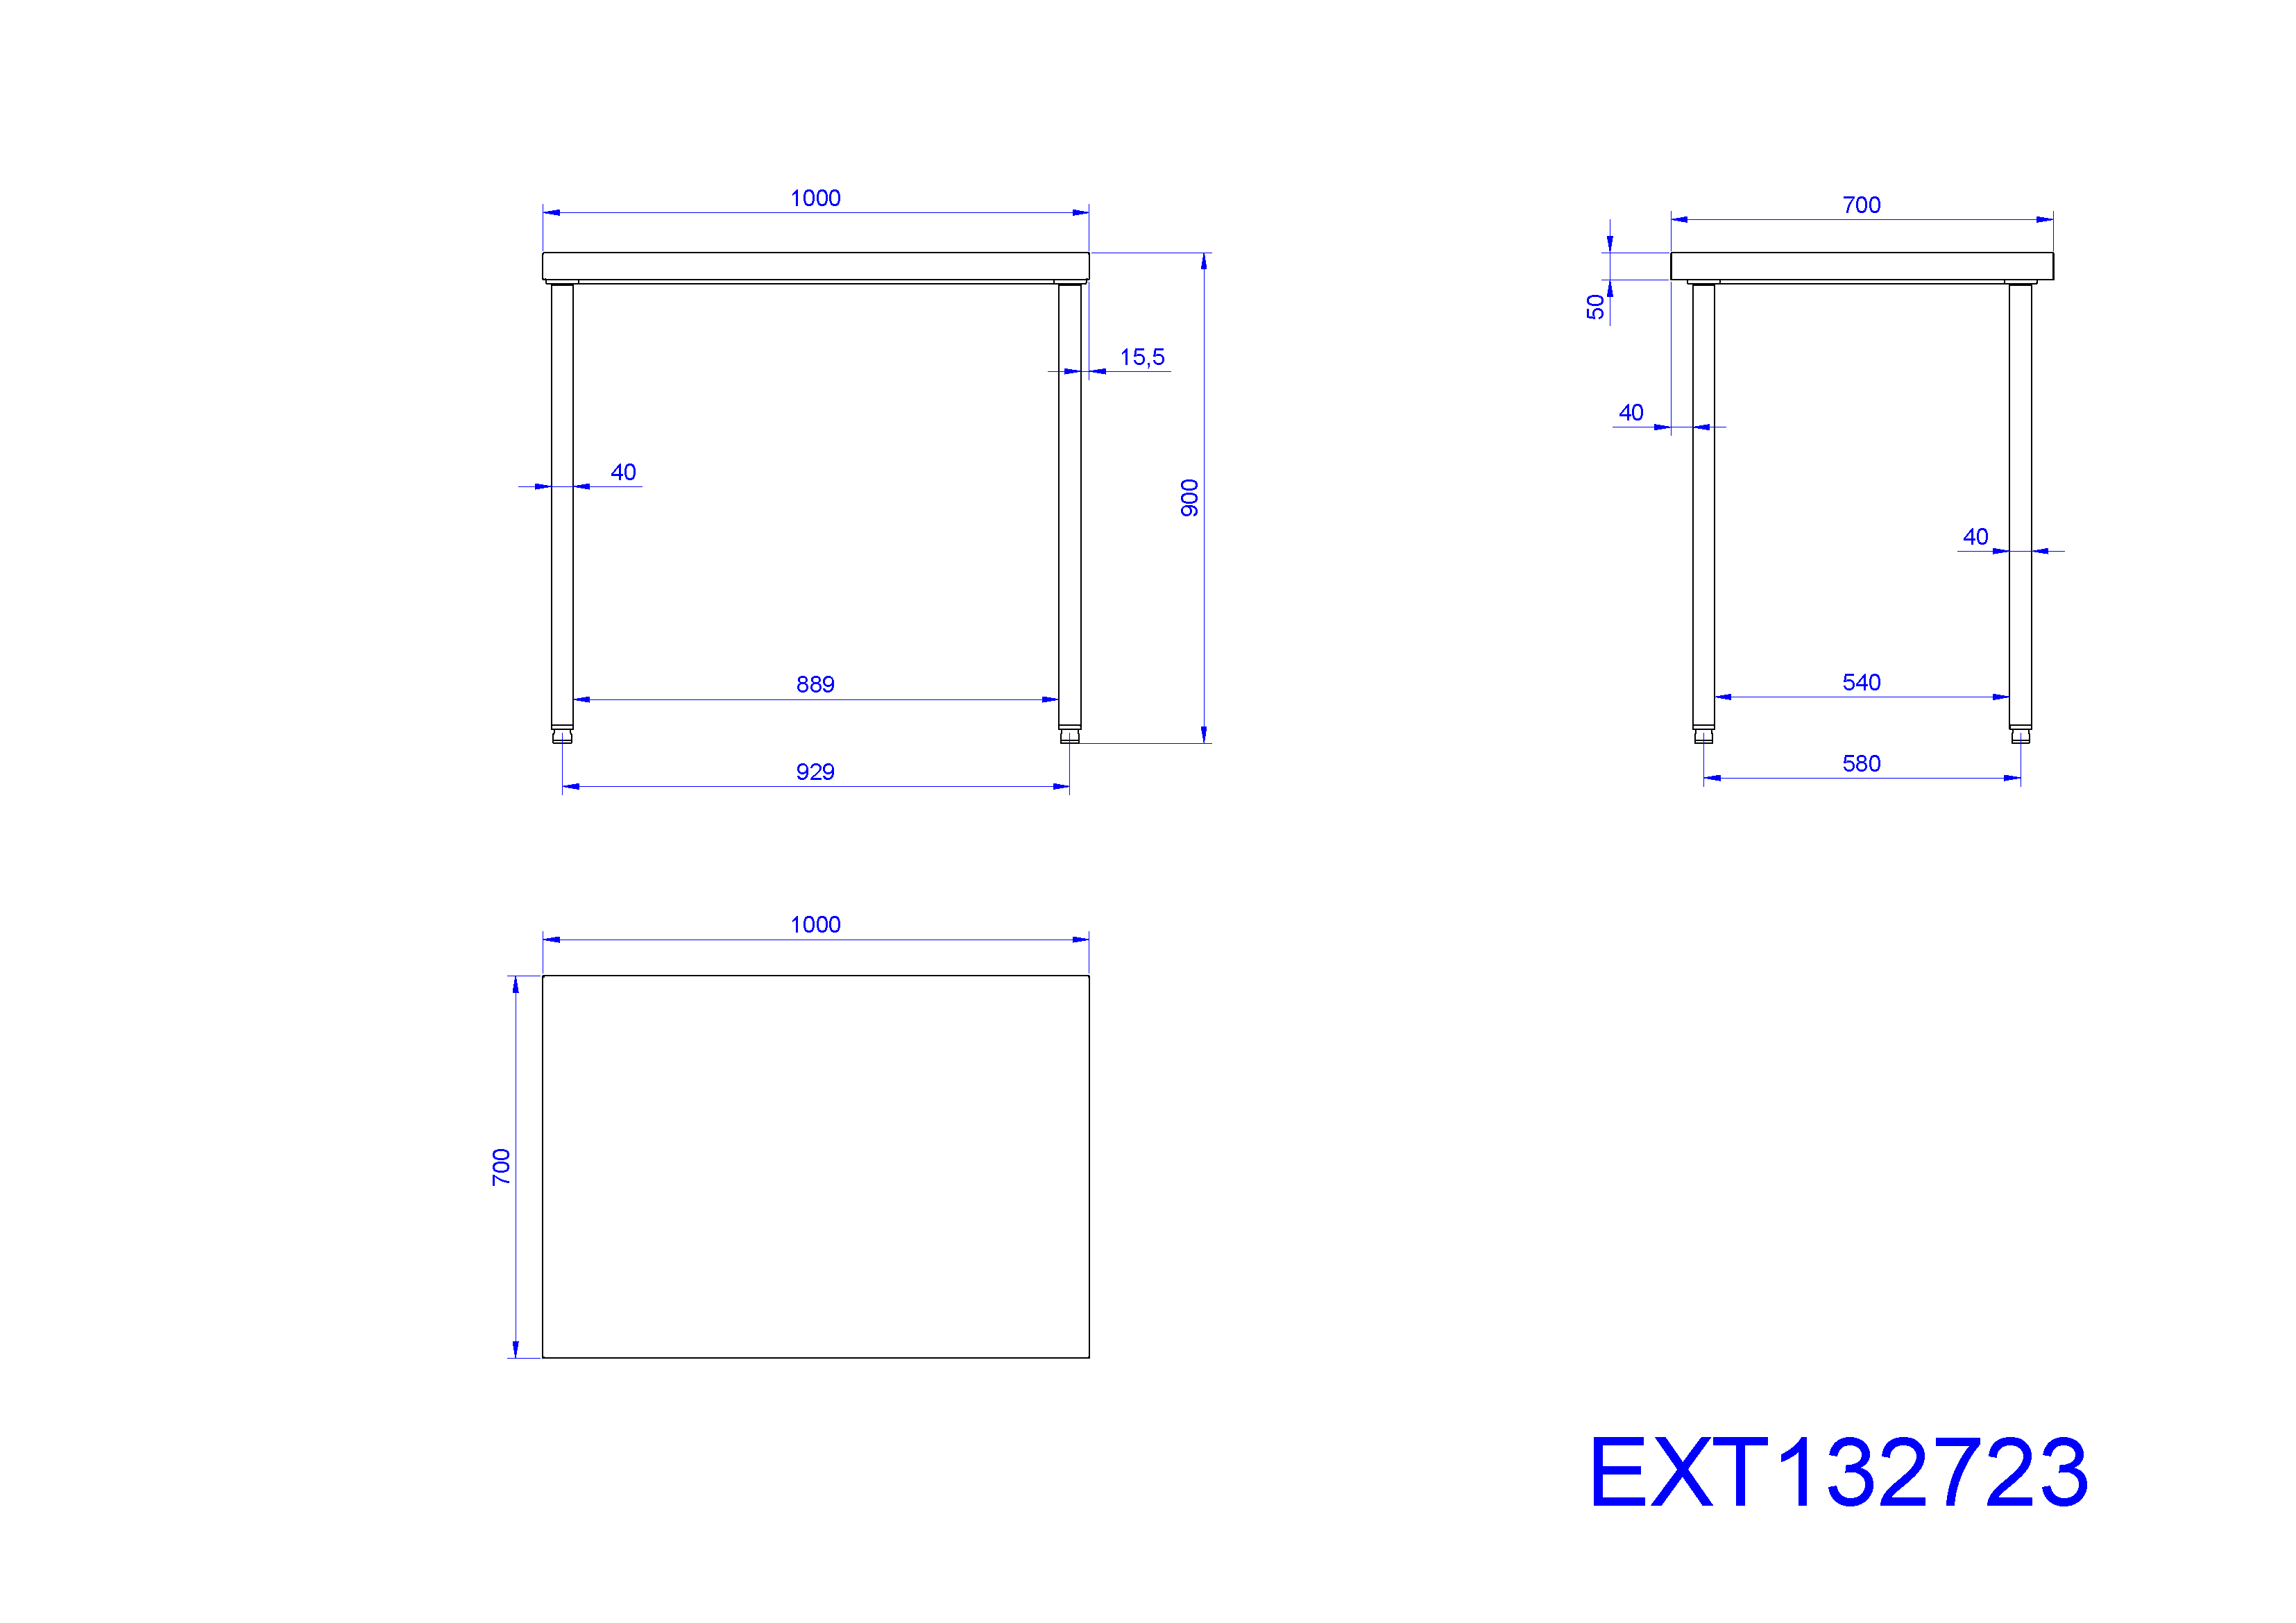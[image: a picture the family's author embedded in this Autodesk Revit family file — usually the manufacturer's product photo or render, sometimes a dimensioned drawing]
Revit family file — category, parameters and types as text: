
# Revit family: QF_ELECTROLUXPROFESSIONAL_132726_TG1600PN
name_source: partatom
category: Attrezzature speciali
units: mm (PartAtom-declared; Revit-internal decimal feet)

## family parameters
Basato su piano di lavoro = No
Condiviso = No
Punto di calcolo locali = No
Quota connettore circolare = Usa diametro
Sempre verticale = Sì
Taglio con vuoti quando caricato = No
Tipo di parte = Normale

## types (1)
- Standard
    Accessory = Sì
    Cold Water Size = 0 mm
    Compressed Air Pressure = 0.0 Pa
    Compressed Air Size = 0 mm
    Compressed Air Volume = 0.0 L/s
    Condensate Return Size = 0 mm
    Cycle = 0 Hz
    Depth Actual = 700 mm  [stored 2.29659 ft]
    Descrizione = WORK TABLE 1600 MM
    Direct Waste Size = 0 mm
    Gas Input Pressure = 0
    Gas KW = 0
    Gas Size = 0 mm
    HP = 0 HP
    Height Actual = 900 mm  [stored 2.95276 ft]
    Hot Water Size = 0 mm
    Item Number = 132726
    Length Actual = 1600 mm  [stored 5.24934 ft]
    Modello = TG1600PN
    Phase = 0
    Produttore = Electrolux Professional
    Prospetto di default = 0 mm  [stored 0 ft]
    Refrigerant Compressor Remote = Sì
    Refrigeration Liquid Line Size = 0 mm  [stored 0 ft]
    Refrigeration Suction Line Size = 0 mm  [stored 0 ft]
    Steam Consumption per Hour = 0
    Steam Supply Maximum Pressure = 0.0 Pa
    Steam Supply Minimum Pressure = 0.0 Pa
    Steam Supply Size = 0 mm
    URL = https://www.electroluxprofessional.com
    URL Manufacturer = https://www.electroluxprofessional.com
    Volts = 0 V
    Watts = 0 W
    Weight = 50.00 kg

note: source unit labels omitted for Gas Input Pressure — the stored unit's dimension contradicts the parameter name (converter mislabeling)

note: [stored X ft] marks values corroborated as IEEE doubles in the binary element streams (Revit-internal decimal feet)

## geometry (parser evidence)
native form markers: Sweep x2
no freeform markers — native parametric forms only
